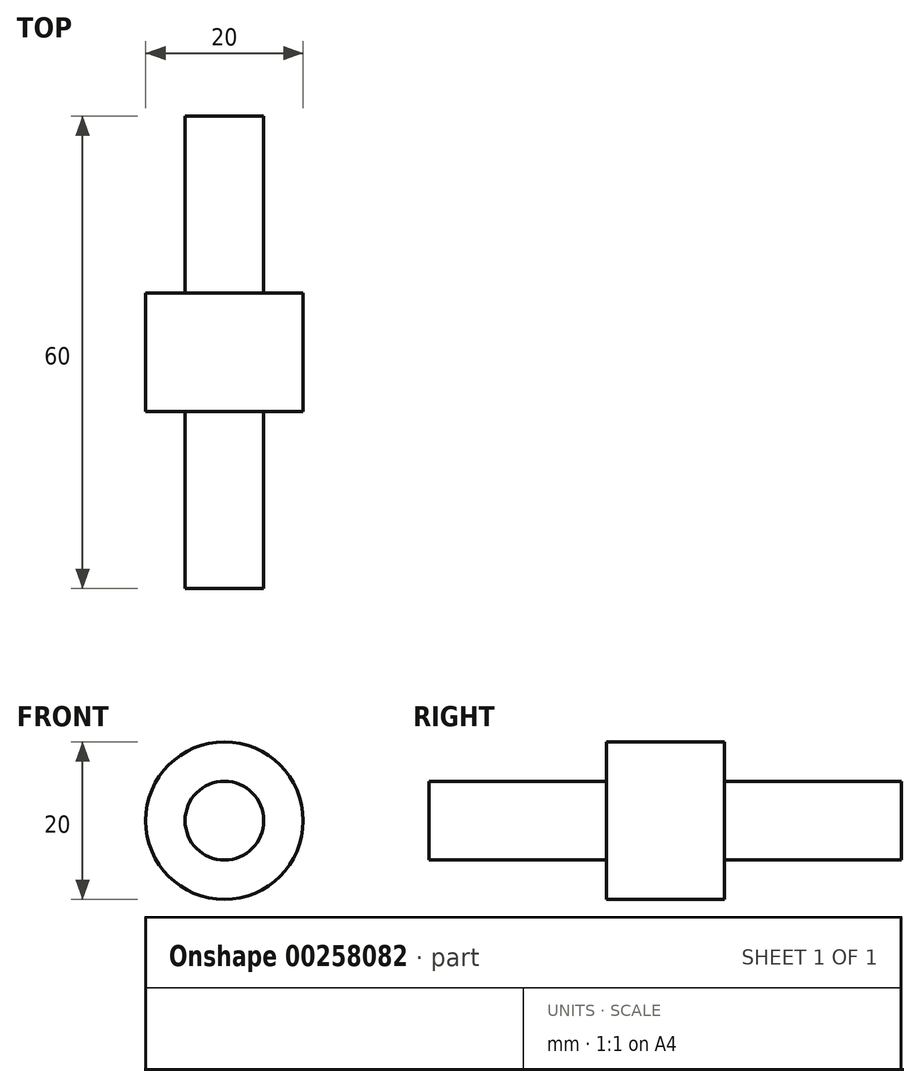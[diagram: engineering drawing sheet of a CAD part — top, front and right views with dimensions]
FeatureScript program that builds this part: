
annotation { "Feature Type Name" : "Feature", "Feature Type Description" : "" }
export const myFeature = defineFeature(function(context is Context, id is Id, definition is map)
    precondition{}
    {
        {
            var Q0;
            Q0=qCreatedBy(makeId("Front.planeOp"),FACE);
            var sketch = newSketch(context, id + "F0", { "sketchPlane" : qUnion([Q0])});
            skCircle(sketch, "E0", {"center": v(0, 0) * mm, "radius": 5 * mm});
            skSolve(sketch);
        }
        {
            var Q0;
            Q0 = qSketchRegion(id + "F0", true);
            extrude(context, id + "F1", {"entities" : qUnion([Q0]), "depth" : 60 * mm, "symmetric" : true});
        }
        {
            var Q0;
            Q0=qCreatedBy(makeId("Front.planeOp"),FACE);
            var sketch = newSketch(context, id + "F2", { "sketchPlane" : qUnion([Q0])});
            skCircle(sketch, "E1", {"center": v(0, 0) * mm, "radius": 10 * mm});
            skSolve(sketch);
        }
        {
            var Q0;
            Q0 = qSketchRegion(id + "F2", true);
            extrude(context, id + "F3", {"entities" : qUnion([Q0]), "operationType" : NewBodyOperationType.ADD, "depth" : 15 * mm, "symmetric" : true});
        }
    });
